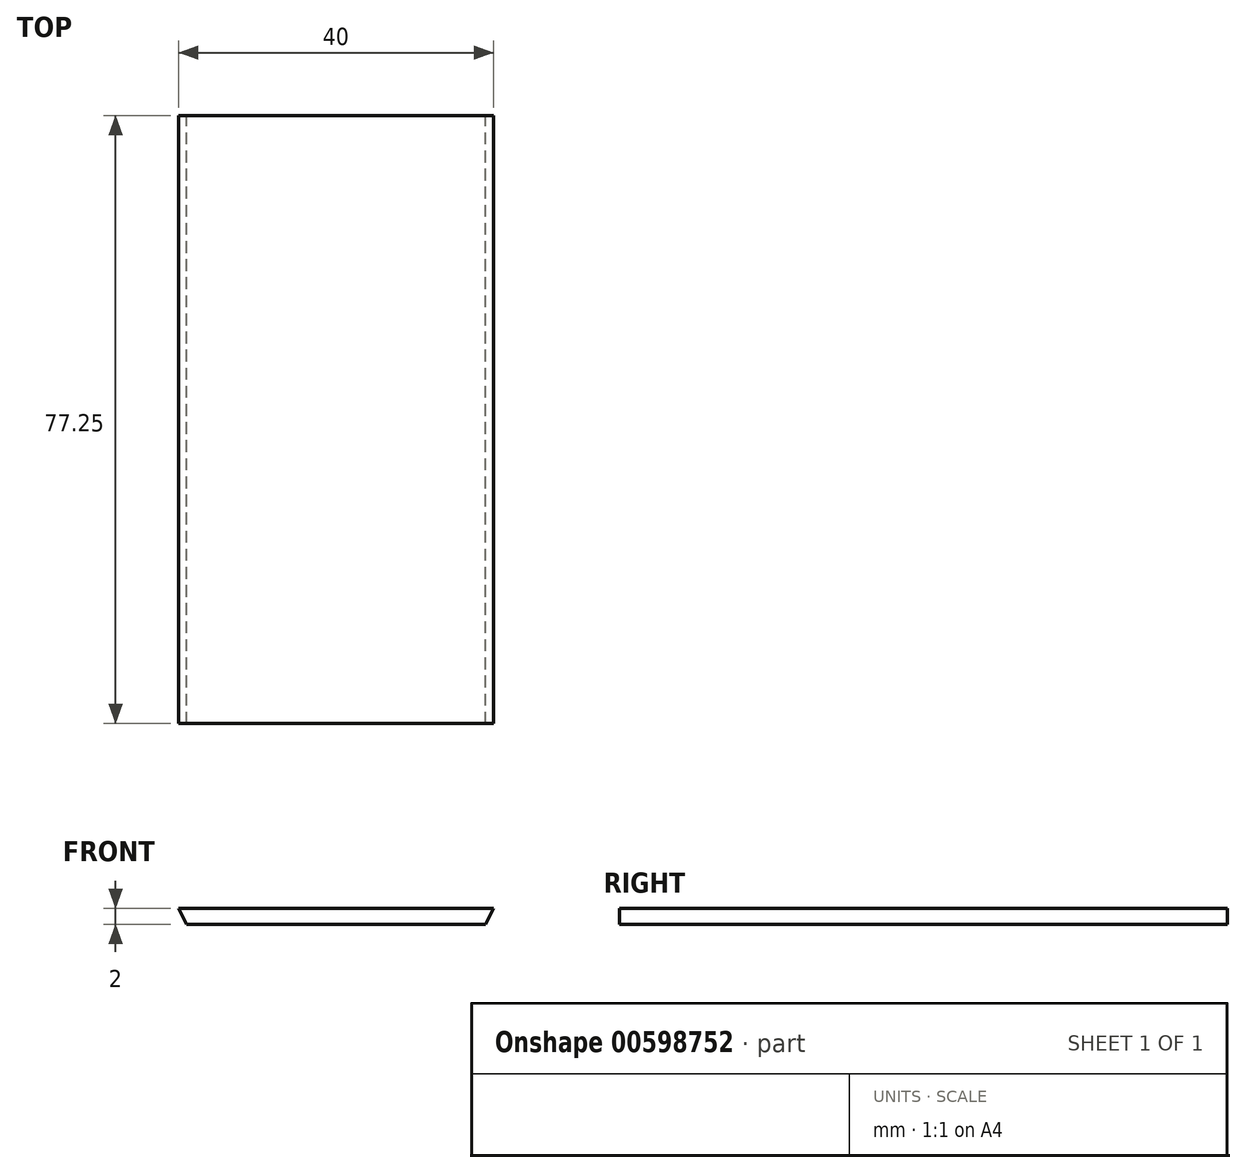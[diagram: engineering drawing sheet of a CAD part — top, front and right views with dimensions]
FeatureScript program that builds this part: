
annotation { "Feature Type Name" : "Feature", "Feature Type Description" : "" }
export const myFeature = defineFeature(function(context is Context, id is Id, definition is map)
    precondition{}
    {
        {
            var Q0;
            Q0=qCreatedBy(makeId("Front.planeOp"),FACE);
            var sketch = newSketch(context, id + "F0", { "sketchPlane" : qUnion([Q0])});
            skLineSegment(sketch, "E0", {"start": v(0, 0) * mm, "end": v(38, 0) * mm});
            skLineSegment(sketch, "E1", {"start": v(19, 0) * mm, "end": v(19, 2) * mm});
            skLineSegment(sketch, "E2", {"start": v(19, 2) * mm, "end": v(-1, 2) * mm});
            skLineSegment(sketch, "E3", {"start": v(19, 2) * mm, "end": v(39, 2) * mm});
            skLineSegment(sketch, "E4", {"start": v(-1, 2) * mm, "end": v(0, 0) * mm});
            skLineSegment(sketch, "E5", {"start": v(38, 0) * mm, "end": v(39, 2) * mm});
            skSolve(sketch);
        }
        {
            var Q0;
            {var subQ2=sQuery(id+"F0.wireOp",EDGE,"E1");Q0=makeQuery(id+"F0.imprint","IMPRINT",FACE,{"disambiguationData":[TD([[makeQuery(id+"F0.imprint","IMPRINT",EDGE,{"derivedFrom":subQ2}),-1.0]])]});}
            var Q1;
            {var subQ2=sQuery(id+"F0.wireOp",EDGE,"E1");Q1=makeQuery(id+"F0.imprint","IMPRINT",FACE,{"disambiguationData":[TD([[makeQuery(id+"F0.imprint","IMPRINT",EDGE,{"derivedFrom":subQ2}),1.0]])]});}
            extrude(context, id + "F1", {"entities" : qUnion([Q0, Q1]), "depth" : 77.25 * mm, "offsetDistance" : 25.4 * mm});
        }
    });
